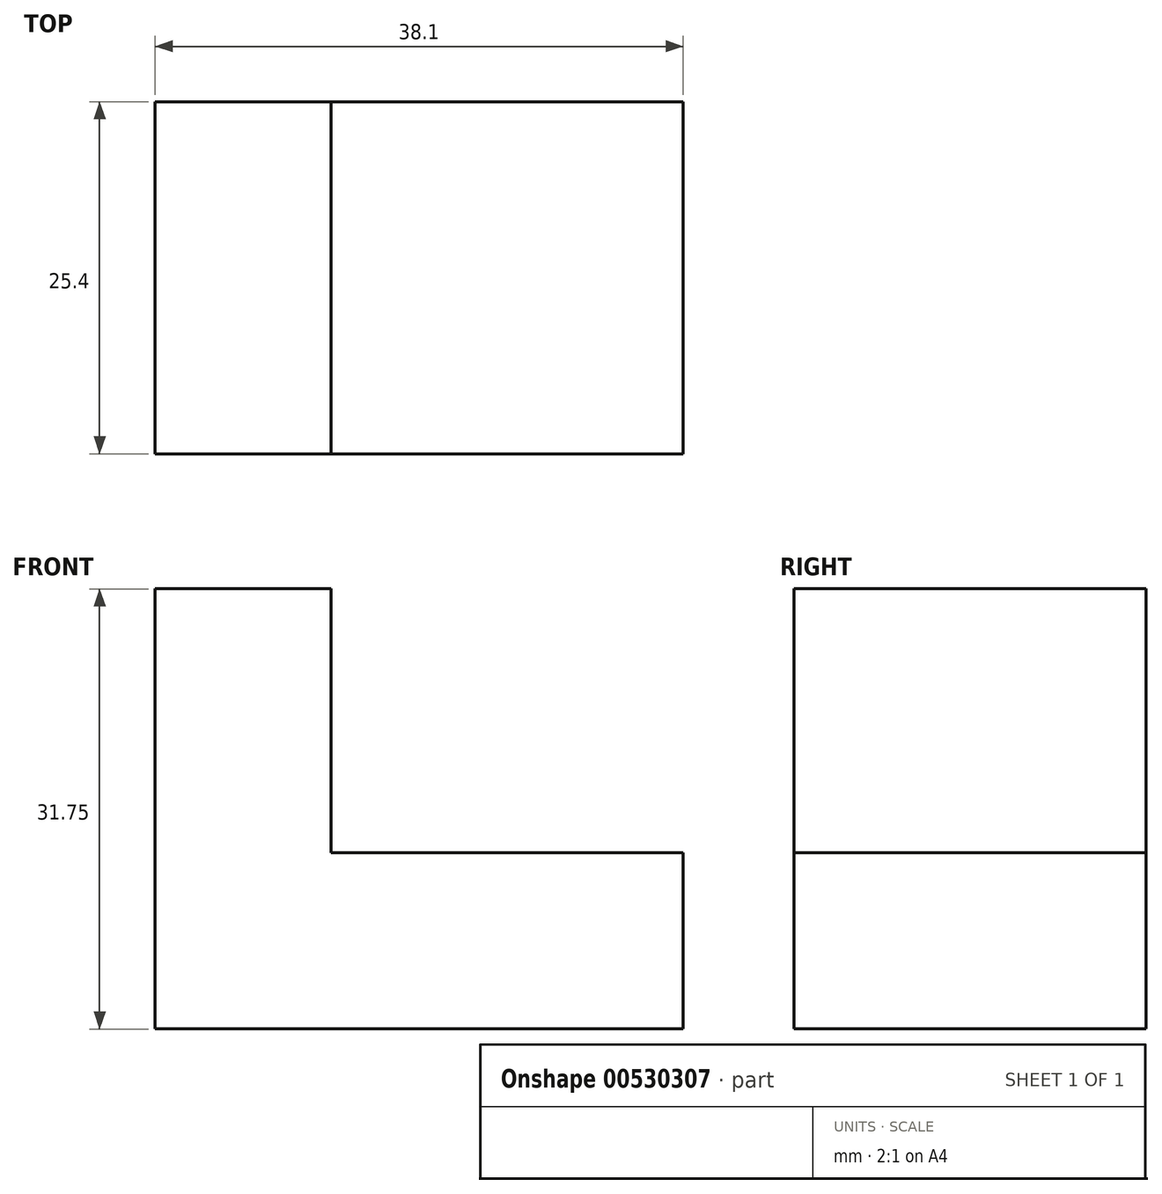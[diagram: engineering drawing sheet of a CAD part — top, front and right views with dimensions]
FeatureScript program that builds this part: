
annotation { "Feature Type Name" : "Feature", "Feature Type Description" : "" }
export const myFeature = defineFeature(function(context is Context, id is Id, definition is map)
    precondition{}
    {
        {
            var Q0;
            Q0=qCreatedBy(makeId("Front.planeOp"),FACE);
            var sketch = newSketch(context, id + "F0", { "sketchPlane" : qUnion([Q0])});
            skLineSegment(sketch, "E0", {"start": v(-57.55, 31.56) * mm, "end": v(-57.55, -0.19) * mm});
            skLineSegment(sketch, "E1", {"start": v(-57.55, -0.19) * mm, "end": v(-19.45, -0.19) * mm});
            skLineSegment(sketch, "E2", {"start": v(-19.45, -0.19) * mm, "end": v(-19.45, 12.51) * mm});
            skLineSegment(sketch, "E3", {"start": v(-19.45, 12.51) * mm, "end": v(-44.85, 12.51) * mm});
            skLineSegment(sketch, "E4", {"start": v(-44.85, 12.51) * mm, "end": v(-44.85, 31.56) * mm});
            skLineSegment(sketch, "E5", {"start": v(-44.85, 31.56) * mm, "end": v(-57.55, 31.56) * mm});
            skSolve(sketch);
        }
        {
            var Q0;
            Q0=makeQuery(id+"F0.imprint","IMPRINT",FACE,{"disambiguationData":[TD([[makeQuery(id+"F0.imprint","IMPRINT",EDGE,{"derivedFrom":sQuery(id+"F0.wireOp",EDGE,"E0")}),1.0]])]});
            extrude(context, id + "F1", {"entities" : qUnion([Q0]), "depth" : 25.4 * mm, "offsetDistance" : 25.4 * mm});
        }
    });
